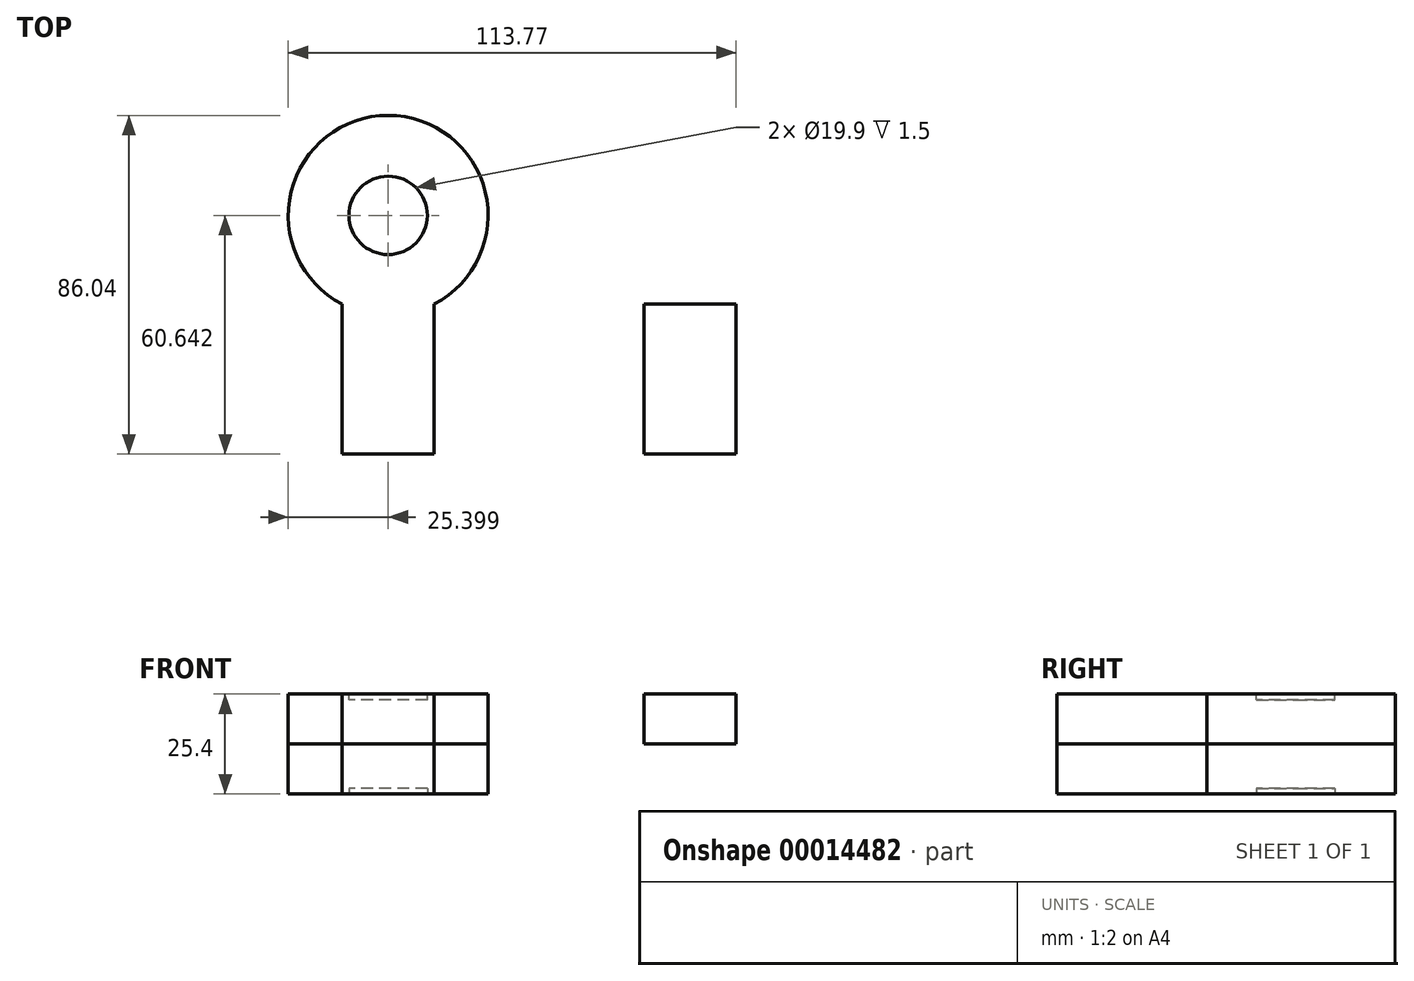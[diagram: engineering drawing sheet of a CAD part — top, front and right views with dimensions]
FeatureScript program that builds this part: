
annotation { "Feature Type Name" : "Feature", "Feature Type Description" : "" }
export const myFeature = defineFeature(function(context is Context, id is Id, definition is map)
    precondition{}
    {
        {
            var Q0;
            Q0=qCreatedBy(makeId("Top.planeOp"),FACE);
            var sketch = newSketch(context, id + "F0", { "sketchPlane" : qUnion([Q0])});
            skLineSegment(sketch, "E0.bottom", {"start": v(-12.09, 0) * mm, "end": v(11.32, 0) * mm});
            skLineSegment(sketch, "E0.top", {"start": v(-12.09, -38.1) * mm, "end": v(11.32, -38.1) * mm});
            skLineSegment(sketch, "E0.left", {"start": v(-12.09, 0) * mm, "end": v(-12.09, -38.1) * mm});
            skLineSegment(sketch, "E0.right", {"start": v(11.32, 0) * mm, "end": v(11.32, -38.1) * mm});
            skArc(sketch, "E1", {"start": v(11.32, 0) * mm, "mid": v(-0.38, 47.94) * mm, "end": v(-12.09, 0) * mm});
            skLineSegment(sketch, "E2", {"start": v(37.95, 69.05) * mm, "end": v(37.95, -86.92) * mm, "construction": true});
            skArc(sketch, "E3.MirrorCS", {"start": v(64.58, 0) * mm, "mid": v(76.29, 47.94) * mm, "end": v(88, 0) * mm});
            skLineSegment(sketch, "E4.MirrorCS", {"start": v(88, 0) * mm, "end": v(64.58, 0) * mm});
            skLineSegment(sketch, "E5.MirrorCS", {"start": v(64.58, 0) * mm, "end": v(64.58, -38.1) * mm});
            skLineSegment(sketch, "E6.MirrorCS", {"start": v(88, 0) * mm, "end": v(88, -38.1) * mm});
            skLineSegment(sketch, "E7.MirrorCS", {"start": v(88, -38.1) * mm, "end": v(64.58, -38.1) * mm});
            skLineSegment(sketch, "E8", {"start": v(-60.1, 41.64) * mm, "end": v(-60.1, -48.62) * mm, "construction": true});
            skSolve(sketch);
        }
        {
            var Q0;
            Q0=makeQuery(id+"F0.imprint","IMPRINT",FACE,{"disambiguationData":[TD([[makeQuery(id+"F0.imprint","IMPRINT",EDGE,{"derivedFrom":sQuery(id+"F0.wireOp",EDGE,"E1")}),1.0]])]});
            var Q1;
            Q1=makeQuery(id+"F0.imprint","IMPRINT",FACE,{"disambiguationData":[TD([[makeQuery(id+"F0.imprint","IMPRINT",EDGE,{"derivedFrom":sQuery(id+"F0.wireOp",EDGE,"E0.top")}),1.0]])]});
            extrude(context, id + "F1", {"entities" : qUnion([Q0, Q1]), "depth" : 12.7 * mm});
        }
        {
            var Q0;
            Q0=makeQuery(id+"F1.opExtrude","CAP_FACE",FACE,{"disambiguationData":[OSD([sQuery(id+"F0.wireOp",EDGE,"E0.top"),sQuery(id+"F0.wireOp",EDGE,"E0.left"),sQuery(id+"F0.wireOp",EDGE,"E0.right"),sQuery(id+"F0.wireOp",EDGE,"E1")])],"isStart":false});
            var sketch = newSketch(context, id + "F2", { "sketchPlane" : qUnion([Q0])});
            skCircle(sketch, "E9", {"center": v(-0.38, 22.54) * mm, "radius": 9.95 * mm});
            skSolve(sketch);
        }
        {
            var Q0;
            Q0=makeQuery(id+"F2.imprint","IMPRINT",FACE,{"disambiguationData":[TD([[makeQuery(id+"F2.imprint","IMPRINT",EDGE,{"derivedFrom":sQuery(id+"F2.wireOp",EDGE,"E9")}),1.0]])]});
            extrude(context, id + "F3", {"entities" : qUnion([Q0]), "operationType" : NewBodyOperationType.REMOVE, "oppositeDirection" : true, "depth" : 1.5 * mm});
        }
        {
            var Q0;
            Q0=makeQuery(id+"F1.opExtrude","CAP_FACE",FACE,{"disambiguationData":[OSD([sQuery(id+"F0.wireOp",EDGE,"E0.top"),sQuery(id+"F0.wireOp",EDGE,"E0.left"),sQuery(id+"F0.wireOp",EDGE,"E0.right"),sQuery(id+"F0.wireOp",EDGE,"E1")])],"isStart":false});
            var sketch = newSketch(context, id + "F4", { "sketchPlane" : qUnion([Q0])});
            skLineSegment(sketch, "E10.bottom", {"start": v(0, 32.49) * mm, "end": v(2.75, 32.49) * mm});
            skLineSegment(sketch, "E10.top", {"start": v(0, 47.75) * mm, "end": v(2.75, 47.75) * mm});
            skLineSegment(sketch, "E10.left", {"start": v(0, 32.49) * mm, "end": v(0, 47.75) * mm});
            skLineSegment(sketch, "E10.right", {"start": v(2.75, 32.49) * mm, "end": v(2.75, 47.75) * mm});
            skSolve(sketch);
        }
        {
            var Q0;
            Q0=sQuery(id+"F4.wireOp",EDGE,"E10.right");
            var Q1;
            Q1=sQuery(id+"F4.wireOp",EDGE,"E10.left");
            var Q2;
            Q2=sQuery(id+"F4.wireOp",EDGE,"E10.bottom");
            var Q3;
            Q3=sQuery(id+"F4.wireOp",EDGE,"E10.top");
            extrude(context, id + "F5", {"bodyType" : ToolBodyType.SURFACE, "surfaceEntities" : qUnion([Q0, Q1, Q2, Q3]), "oppositeDirection" : true, "depth" : 1 * mm});
        }
        {
            var Q0;
            Q0=makeQuery(id+"F0.imprint","IMPRINT",FACE,{"disambiguationData":[TD([[makeQuery(id+"F0.imprint","IMPRINT",EDGE,{"derivedFrom":sQuery(id+"F0.wireOp",EDGE,"E4.MirrorCS")}),1.0]])]});
            var Q1;
            Q1=makeQuery(id+"F0.imprint","IMPRINT",FACE,{"disambiguationData":[TD([[makeQuery(id+"F0.imprint","IMPRINT",EDGE,{"derivedFrom":sQuery(id+"F0.wireOp",EDGE,"E3.MirrorCS")}),-1.0]])]});
            extrude(context, id + "F6", {"entities" : qUnion([Q0, Q1]), "depth" : 12.7 * mm});
        }
        {
            var Q0;
            Q0=makeQuery(id+"F1.opExtrude","SWEPT_BODY",BODY,{"disambiguationData":[OSD([sQuery(id+"F0.wireOp",EDGE,"E0.top"),sQuery(id+"F0.wireOp",EDGE,"E0.left"),sQuery(id+"F0.wireOp",EDGE,"E0.right"),sQuery(id+"F0.wireOp",EDGE,"E1")])]});
            var Q1;
            Q1=makeQuery(id+"F5.opExtrude","SWEPT_BODY",BODY,{"disambiguationData":[OSD([sQuery(id+"F4.wireOp",EDGE,"E10.top")])]});
            var Q2;
            Q2=qCreatedBy(makeId("Top.planeOp"),FACE);
            mirror(context, id + "F7", {"operationType" : NewBodyOperationType.ADD, "entities" : qUnion([Q0, Q1]), "mirrorPlane" : qUnion([Q2])});
        }
    });
